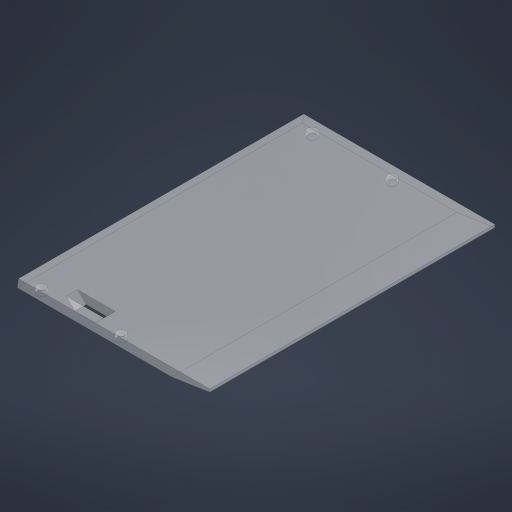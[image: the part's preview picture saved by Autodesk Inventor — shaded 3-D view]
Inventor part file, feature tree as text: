
AUTODESK INVENTOR PART (.ipt)
format: ipt  version: 2024 (Build 280153000, 153)  size: 220,160 bytes
history: native  units: in
note: dims shown in document units (in); Inventor stores cm internally (conversion verified against a paired STEP export)
features: extrude x3, sketch x3, chamfer x1
ambient origin geometry x8: Origin, YZ Plane, XZ Plane, XY Plane, X Axis, Y Axis, Z Axis, Center Point
bodies: Solid1 (feature_tree)
feature tree (7):
  extrude  "Extrusion1"  Depth=3.937in TaperAngle=0.0deg
  extrude  "Extrusion2"  Depth=0.1181in TaperAngle=45.0deg
  chamfer  "Chamfer2"  Distance=0.0394in
  extrude  "Extrusion3"  Depth=0.1181in
  sketch  "Sketch1"  dims[d0=2.6378in d1=3.937in d2=0.0in]
  sketch  "Sketch3"  dims[d21=0.0in d22=0.0in d23=0.1181in d24=0.0787in d25=45.0deg]
  sketch  "Sketch4"  dims[d26=0.1181in d27=0.0394in d28=0.1181in d29=0.1181in d30=0.1181in d31=0.1181in d32=0.0984in d33=0.0984in d34=0.0984in d35=0.0984in d36=0.2362in d37=1.1024in d38=0.2362in d39=1.1024in d40=0.0787in d41=0.0in d46=0.0192in d48=0.5231in]
